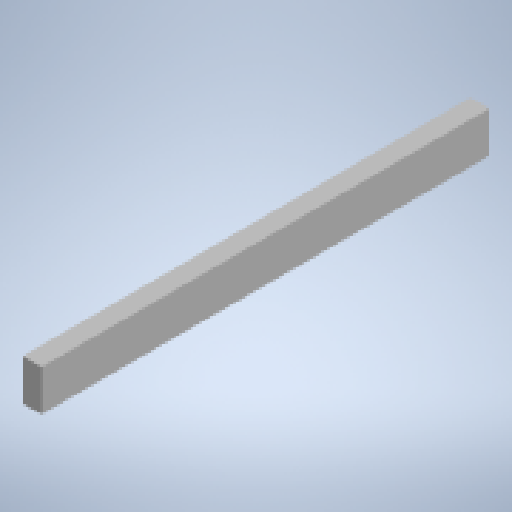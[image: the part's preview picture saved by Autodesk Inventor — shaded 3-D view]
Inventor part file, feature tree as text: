
AUTODESK INVENTOR PART (.ipt)
format: ipt  version: 2023 (Build 270158000, 158)  size: 128,000 bytes
history: native  units: in
note: dims shown in document units (in); Inventor stores cm internally (conversion verified against a paired STEP export)
features: extrude x1, sketch x1
ambient origin geometry x8: Origin, YZ Plane, XZ Plane, XY Plane, X Axis, Y Axis, Z Axis, Center Point
bodies: Solid1 (feature_tree)
feature tree (2):
  extrude  "Extrusion1"  Depth=3.75in
  sketch  "Sketch1"  dims[d0=1.75in d1=3.75in d2=41.0in d3=0.0in]
